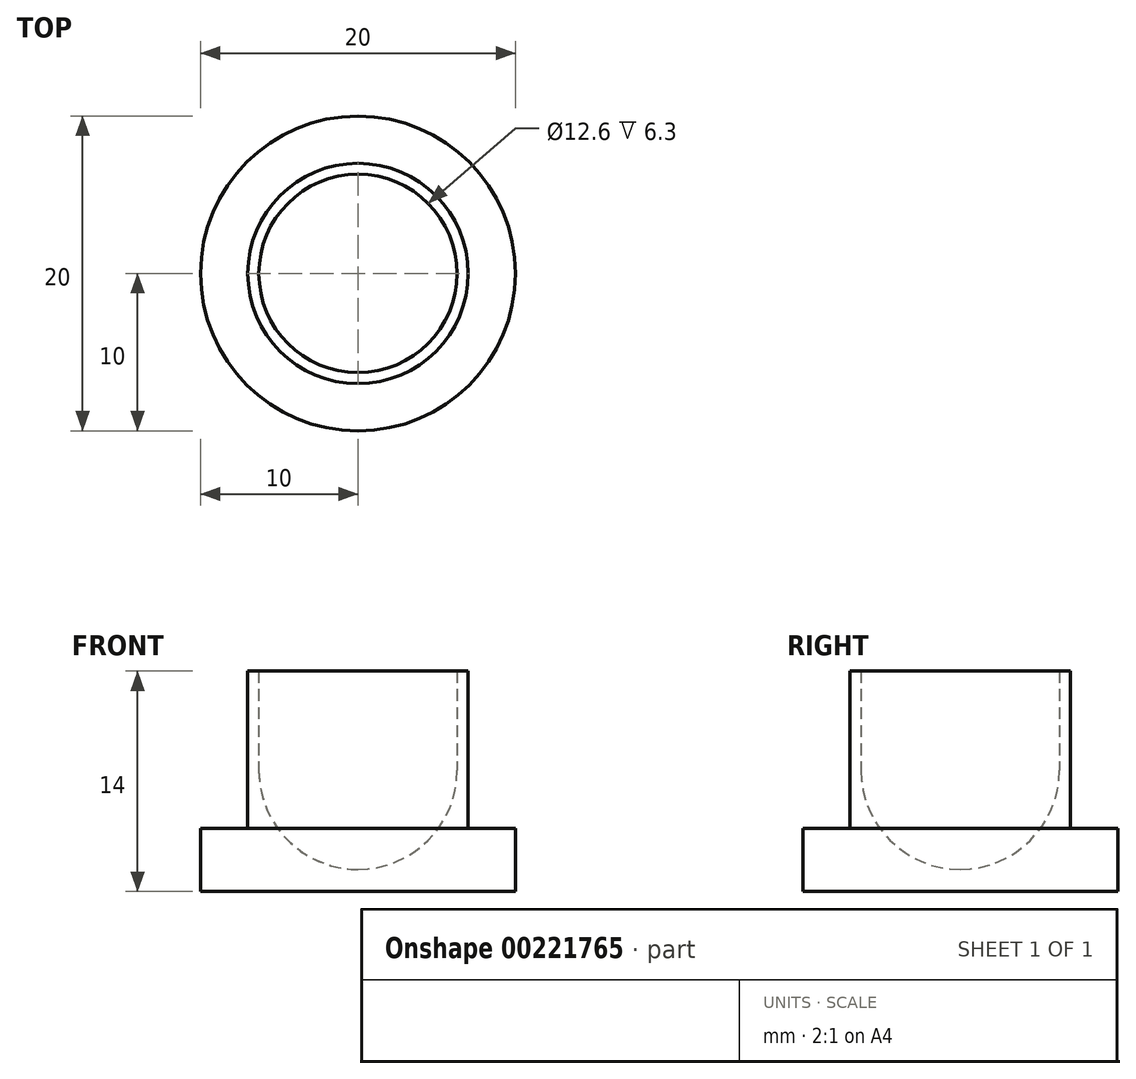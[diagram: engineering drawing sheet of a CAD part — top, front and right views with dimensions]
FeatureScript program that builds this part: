
annotation { "Feature Type Name" : "Feature", "Feature Type Description" : "" }
export const myFeature = defineFeature(function(context is Context, id is Id, definition is map)
    precondition{}
    {
        {
            var Q0;
            Q0=qCreatedBy(makeId("Top.planeOp"),FACE);
            var sketch = newSketch(context, id + "F0", { "sketchPlane" : qUnion([Q0])});
            skCircle(sketch, "E0", {"center": v(0, 0) * mm, "radius": 6 * mm, "construction": true});
            skCircle(sketch, "E1", {"center": v(0, 0) * mm, "radius": 10 * mm});
            skSolve(sketch);
        }
        {
            var Q0;
            Q0 = qSketchRegion(id + "F0", true);
            var Q1;
            Q1=sQuery(id+"F0.wireOp",EDGE,"E0");
            extrude(context, id + "F1", {"entities" : qUnion([Q0]), "surfaceEntities" : qUnion([Q1]), "depth" : 14 * mm});
        }
        {
            var Q0;
            Q0=qCreatedBy(makeId("Front.planeOp"),FACE);
            var sketch = newSketch(context, id + "F2", { "sketchPlane" : qUnion([Q0])});
            skLineSegment(sketch, "E2.bottom", {"start": v(0, 14) * mm, "end": v(6.3, 14) * mm});
            skLineSegment(sketch, "E2.top", {"start": v(0, 7.7) * mm, "end": v(6.3, 7.7) * mm});
            skLineSegment(sketch, "E2.left", {"start": v(0, 14) * mm, "end": v(0, 7.7) * mm});
            skLineSegment(sketch, "E2.right", {"start": v(6.3, 14) * mm, "end": v(6.3, 7.7) * mm});
            skArc(sketch, "E3", {"start": v(0, 1.4) * mm, "mid": v(4.45, 3.25) * mm, "end": v(6.3, 7.7) * mm});
            skLineSegment(sketch, "E4", {"start": v(0, 1.4) * mm, "end": v(0, 7.7) * mm});
            skSolve(sketch);
        }
        {
            var Q0;
            Q0 = qSketchRegion(id + "F2", true);
            var Q1;
            Q1=makeQuery(id+"F1.opExtrude","SWEPT_FACE",FACE,{"disambiguationData":[OSD([sQuery(id+"F0.wireOp",EDGE,"E1")])]});
            revolve(context, id + "F3", {"operationType" : NewBodyOperationType.REMOVE, "entities" : qUnion([Q0]), "axis" : qUnion([Q1]), "revolveType" : RevolveType.FULL, "oppositeDirection" : true});
        }
        {
            var Q0;
            Q0=makeQuery(id+"F1.opExtrude","CAP_FACE",FACE,{"disambiguationData":[OSD([sQuery(id+"F0.wireOp",EDGE,"E1")])],"isStart":false});
            var sketch = newSketch(context, id + "F4", { "sketchPlane" : qUnion([Q0])});
            skCircle(sketch, "E5", {"center": v(0, 0) * mm, "radius": 7 * mm});
            skSolve(sketch);
        }
        {
            var Q0;
            Q0=makeQuery(id+"F4.imprint","IMPRINT",FACE,{"disambiguationData":[TD([[makeQuery(id+"F4.imprint","IMPRINT",EDGE,{"derivedFrom":sQuery(id+"F4.wireOp",EDGE,"E5")}),-1.0]])]});
            extrude(context, id + "F5", {"entities" : qUnion([Q0]), "operationType" : NewBodyOperationType.REMOVE, "oppositeDirection" : true, "depth" : 10 * mm});
        }
    });
